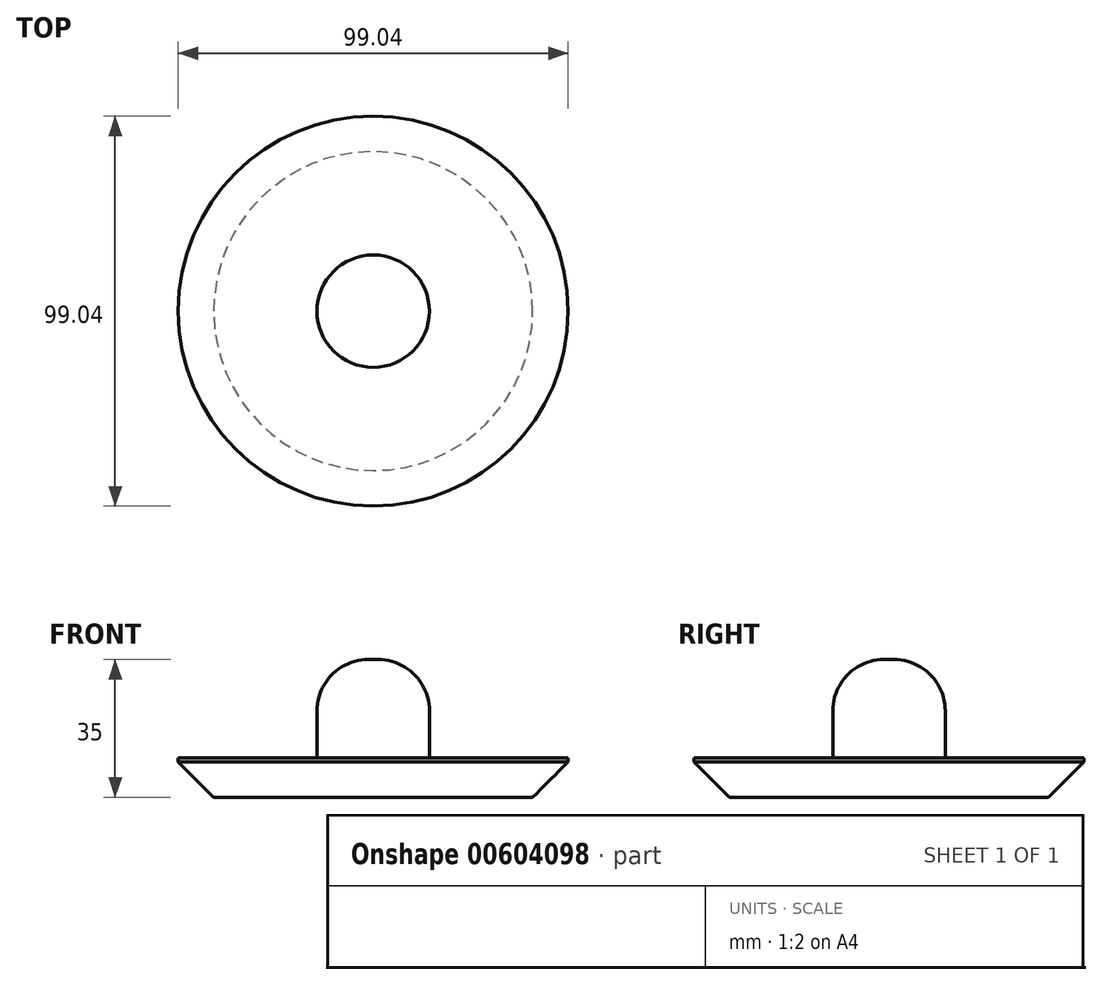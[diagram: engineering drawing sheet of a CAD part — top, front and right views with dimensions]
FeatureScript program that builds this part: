
annotation { "Feature Type Name" : "Feature", "Feature Type Description" : "" }
export const myFeature = defineFeature(function(context is Context, id is Id, definition is map)
    precondition{}
    {
        {
            var Q0;
            Q0=qCreatedBy(makeId("Top.planeOp"),FACE);
            var sketch = newSketch(context, id + "F0", { "sketchPlane" : qUnion([Q0])});
            skCircle(sketch, "E0", {"center": v(0, 0) * mm, "radius": 49.52 * mm});
            skSolve(sketch);
        }
        {
            var Q0;
            Q0=makeQuery(id+"F0.imprint","IMPRINT",FACE,{"disambiguationData":[TD([[makeQuery(id+"F0.imprint","IMPRINT",EDGE,{"derivedFrom":sQuery(id+"F0.wireOp",EDGE,"E0")}),1.0]])]});
            extrude(context, id + "F1", {"entities" : qUnion([Q0]), "depth" : 10 * mm, "offsetDistance" : 25 * mm});
        }
        {
            var Q0;
            Q0=makeQuery(id+"F1.opExtrude","CAP_FACE",FACE,{"disambiguationData":[OSD([sQuery(id+"F0.wireOp",EDGE,"E0")])],"isStart":false});
            var sketch = newSketch(context, id + "F2", { "sketchPlane" : qUnion([Q0])});
            skCircle(sketch, "E1", {"center": v(0, 0) * mm, "radius": 14.29 * mm});
            skSolve(sketch);
        }
        {
            var Q0;
            Q0=makeQuery(id+"F2.imprint","IMPRINT",FACE,{"disambiguationData":[TD([[makeQuery(id+"F2.imprint","IMPRINT",EDGE,{"derivedFrom":sQuery(id+"F2.wireOp",EDGE,"E1")}),1.0]])]});
            extrude(context, id + "F3", {"entities" : qUnion([Q0]), "operationType" : NewBodyOperationType.ADD, "depth" : 25 * mm, "offsetDistance" : 25 * mm});
        }
        {
            var Q0;
            Q0=makeQuery(id+"F3.opExtrude","CAP_FACE",FACE,{"disambiguationData":[OSD([sQuery(id+"F2.wireOp",EDGE,"E1")])],"isStart":false});
            fillet(context, id + "F4", {"entities" : qUnion([Q0]), "radius" : 13.04 * mm, "tangentPropagation" : true, "allowEdgeOverflow" : false});
        }
        {
            var Q0;
            Q0=makeQuery(id+"F1.opExtrude","CAP_EDGE",EDGE,{"disambiguationData":[OSD([sQuery(id+"F0.wireOp",EDGE,"E0")])],"isStart":true});
            chamfer(context, id + "F5", {"entities" : qUnion([Q0]), "width" : 9 * mm, "tangentPropagation" : true});
        }
    });
